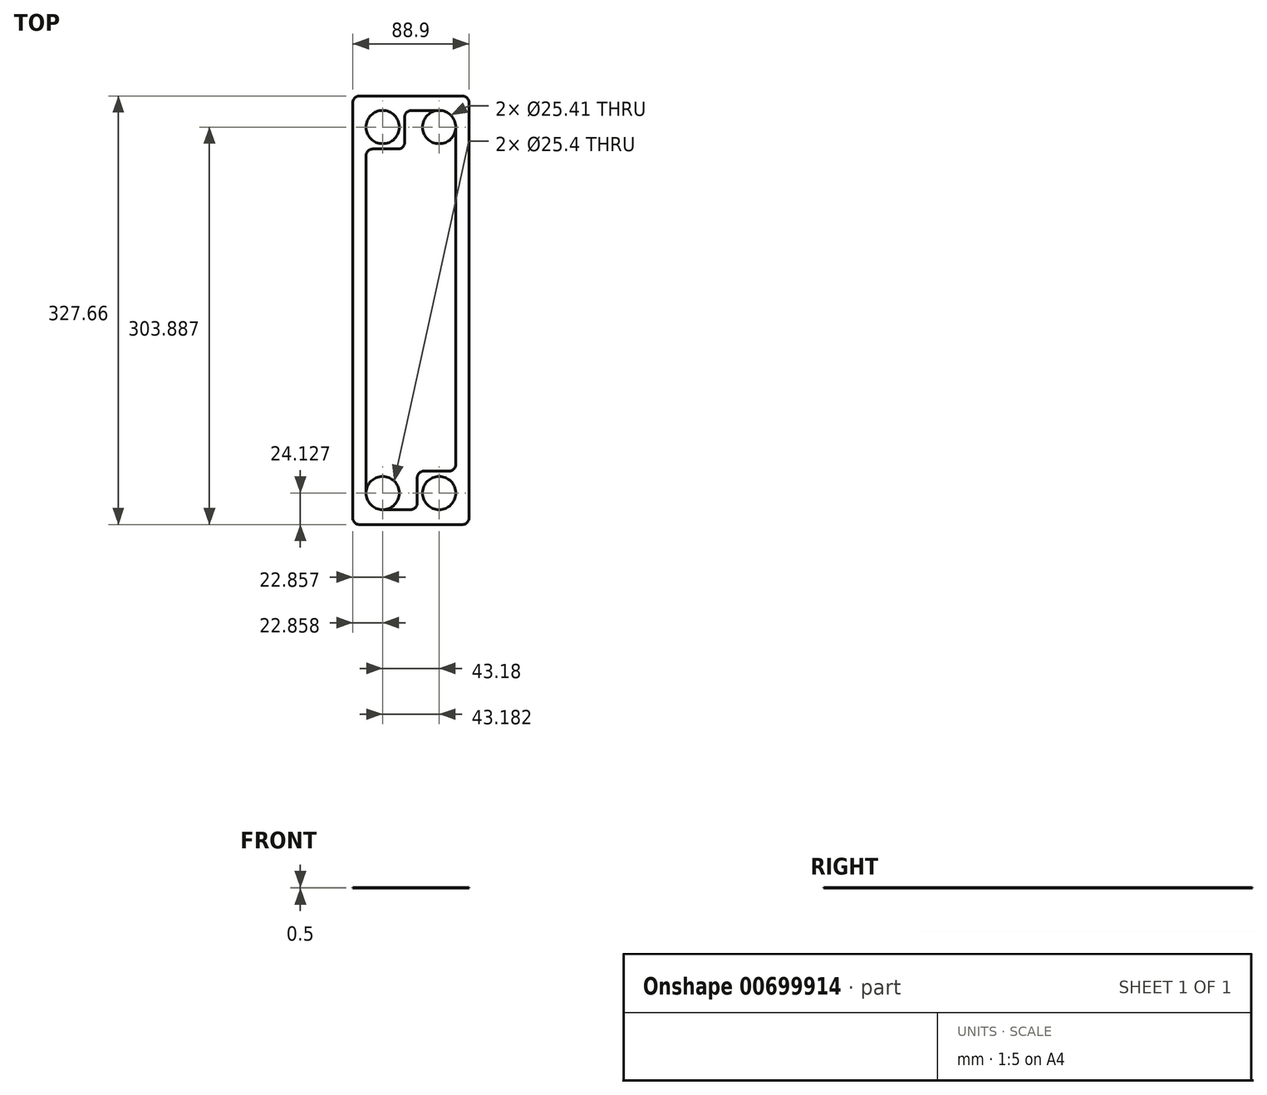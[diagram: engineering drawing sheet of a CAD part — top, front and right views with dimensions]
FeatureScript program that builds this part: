
annotation { "Feature Type Name" : "Feature", "Feature Type Description" : "" }
export const myFeature = defineFeature(function(context is Context, id is Id, definition is map)
    precondition{}
    {
        {
            var Q0;
            Q0=qCreatedBy(makeId("Top.planeOp"),FACE);
            var sketch = newSketch(context, id + "F0", { "sketchPlane" : qUnion([Q0])});
            skLineSegment(sketch, "E0.bottom", {"start": v(28.45, 189.88) * mm, "end": v(-60.45, 189.88) * mm});
            skLineSegment(sketch, "E0.top", {"start": v(28.45, -137.78) * mm, "end": v(-60.45, -137.78) * mm});
            skLineSegment(sketch, "E0.left", {"start": v(28.45, 189.88) * mm, "end": v(28.45, -137.78) * mm});
            skLineSegment(sketch, "E0.right", {"start": v(-60.45, 189.88) * mm, "end": v(-60.45, -137.78) * mm});
            skPoint(sketch, "E1", {"position": v(-37.6, 165.75) * mm});
            skPoint(sketch, "E2", {"position": v(5.59, 165.75) * mm});
            skPoint(sketch, "E3", {"position": v(-34.64, -113.65) * mm});
            skCircle(sketch, "E4.MirrorC", {"center": v(5.59, 166.1) * mm, "radius": 12.7 * mm});
            skCircle(sketch, "E5.MirrorC", {"center": v(-37.6, -113.65) * mm, "radius": 12.7 * mm});
            skCircle(sketch, "E6.MirrorC", {"center": v(-37.6, 166.1) * mm, "radius": 12.7 * mm});
            skCircle(sketch, "E7.MirrorC", {"center": v(5.59, -113.65) * mm, "radius": 12.7 * mm});
            skLineSegment(sketch, "E8", {"start": v(18.3, -96.89) * mm, "end": v(-11.18, -96.89) * mm});
            skLineSegment(sketch, "E9", {"start": v(-11.18, -96.89) * mm, "end": v(-11.18, -126.35) * mm});
            skLineSegment(sketch, "E10", {"start": v(-37.6, -126.35) * mm, "end": v(-11.18, -126.35) * mm});
            skLineSegment(sketch, "E11", {"start": v(18.3, 166.1) * mm, "end": v(18.3, -96.89) * mm});
            skLineSegment(sketch, "E12", {"start": v(5.59, 178.81) * mm, "end": v(-20.83, 178.81) * mm});
            skLineSegment(sketch, "E13", {"start": v(-50.3, -113.65) * mm, "end": v(-50.3, 149.34) * mm});
            skLineSegment(sketch, "E14", {"start": v(-50.3, 149.34) * mm, "end": v(-20.83, 149.34) * mm});
            skLineSegment(sketch, "E15", {"start": v(-20.83, 149.34) * mm, "end": v(-20.83, 178.81) * mm});
            skSolve(sketch);
        }
        {
            var Q0;
            Q0=makeQuery(id+"F0.imprint","IMPRINT",FACE,{"disambiguationData":[TD([[makeQuery(id+"F0.imprint","IMPRINT",EDGE,{"derivedFrom":sQuery(id+"F0.wireOp",EDGE,"E0.bottom")}),1.0]])]});
            var Q1;
            {var subQ13=sQuery(id+"F0.wireOp",EDGE,"E0.left");Q1=makeQuery(id+"F0.imprint","IMPRINT",FACE,{"disambiguationData":[TD([[makeQuery(id+"F0.imprint","IMPRINT",EDGE,{"derivedFrom":subQ13}),-1.0]])]});}
            extrude(context, id + "F1", {"entities" : qUnion([Q0, Q1]), "depth" : 0.5 * mm, "offsetDistance" : 25.4 * mm});
        }
        {
            var Q0;
            {var subQ0=sQuery(id+"F0.wireOp",EDGE,"AVYuMERg-jp42-uW1U-rRQy-gQwv37M2Fl3g");Q0=makeQuery(id+"F0.imprint","IMPRINT",FACE,{"disambiguationData":[TD([[makeQuery(id+"F0.imprint","IMPRINT",EDGE,{"derivedFrom":subQ0}),-1.0]])]});}
            var Q1;
            {var subQ5=sQuery(id+"F0.wireOp",EDGE,"oEbkACiK-kKTr-xMsP-6Dwb-FVCRsFg3JczW");Q1=makeQuery(id+"F0.imprint","IMPRINT",FACE,{"disambiguationData":[TD([[makeQuery(id+"F0.imprint","IMPRINT",EDGE,{"derivedFrom":subQ5}),1.0]])]});}
            var Q2;
            Q2=makeQuery(id+"F0.imprint","IMPRINT",FACE,{"disambiguationData":[TD([[makeQuery(id+"F0.imprint","IMPRINT",EDGE,{"derivedFrom":sQuery(id+"F0.wireOp",EDGE,"E8")}),-1.0]])]});
            extrude(context, id + "F2", {"entities" : qUnion([Q0, Q1, Q2]), "operationType" : NewBodyOperationType.ADD, "depth" : 0 * mm, "offsetDistance" : 25.4 * mm});
        }
        {
            var Q0;
            Q0=makeQuery(id+"F1.opExtrude","SWEPT_EDGE",EDGE,{"disambiguationData":[OSD([sQuery(id+"F0.wireOp",EDGE,"E0.bottom"),sQuery(id+"F0.wireOp",EDGE,"E0.left")])]});
            var Q1;
            Q1=makeQuery(id+"F1.opExtrude","SWEPT_EDGE",EDGE,{"disambiguationData":[OSD([sQuery(id+"F0.wireOp",EDGE,"E0.bottom"),sQuery(id+"F0.wireOp",EDGE,"E0.right")])]});
            var Q2;
            Q2=makeQuery(id+"F1.opExtrude","SWEPT_EDGE",EDGE,{"disambiguationData":[OSD([sQuery(id+"F0.wireOp",EDGE,"E0.top"),sQuery(id+"F0.wireOp",EDGE,"E0.right")])]});
            var Q3;
            Q3=makeQuery(id+"F1.opExtrude","SWEPT_EDGE",EDGE,{"disambiguationData":[OSD([sQuery(id+"F0.wireOp",EDGE,"E0.top"),sQuery(id+"F0.wireOp",EDGE,"E0.left")])]});
            var Q4;
            Q4=makeQuery(id+"F1.opExtrude","SWEPT_EDGE",EDGE,{"disambiguationData":[OSD([sQuery(id+"F0.wireOp",EDGE,"E8"),sQuery(id+"F0.wireOp",EDGE,"E11")])]});
            var Q5;
            Q5=makeQuery(id+"F1.opExtrude","SWEPT_EDGE",EDGE,{"disambiguationData":[OSD([sQuery(id+"F0.wireOp",EDGE,"E8"),sQuery(id+"F0.wireOp",EDGE,"E9")])]});
            var Q6;
            Q6=makeQuery(id+"F1.opExtrude","SWEPT_EDGE",EDGE,{"disambiguationData":[OSD([sQuery(id+"F0.wireOp",EDGE,"E9"),sQuery(id+"F0.wireOp",EDGE,"E10")])]});
            fillet(context, id + "F3", {"entities" : qUnion([Q0, Q1, Q2, Q3, Q4, Q5, Q6]), "radius" : 5.08 * mm, "tangentPropagation" : true, "allowEdgeOverflow" : false});
        }
        {
            var Q0;
            Q0=makeQuery(id+"F1.opExtrude","SWEPT_EDGE",EDGE,{"disambiguationData":[OSD([sQuery(id+"F0.wireOp",EDGE,"oEbkACiK-kKTr-xMsP-6Dwb-FVCRsFg3JczW"),sQuery(id+"F0.wireOp",EDGE,"vKtCIPza-yhRZ-rxRL-Lj7m-7o7ZUmddPepn")])]});
            var Q1;
            Q1=makeQuery(id+"F1.opExtrude","SWEPT_EDGE",EDGE,{"disambiguationData":[OSD([sQuery(id+"F0.wireOp",EDGE,"AVYuMERg-jp42-uW1U-rRQy-gQwv37M2Fl3g"),sQuery(id+"F0.wireOp",EDGE,"vKtCIPza-yhRZ-rxRL-Lj7m-7o7ZUmddPepn")])]});
            var Q2;
            Q2=makeQuery(id+"F1.opExtrude","SWEPT_EDGE",EDGE,{"disambiguationData":[OSD([sQuery(id+"F0.wireOp",EDGE,"pewF66kG-GFMI-JF1X-qAcm-Nm4R1YAsbT13"),sQuery(id+"F0.wireOp",EDGE,"7d1wvmCj-EUQr-oUGu-HAwH-GT3x7ygtlY4H")])]});
            var Q3;
            Q3=makeQuery(id+"F1.opExtrude","SWEPT_EDGE",EDGE,{"disambiguationData":[OSD([sQuery(id+"F0.wireOp",EDGE,"E14"),sQuery(id+"F0.wireOp",EDGE,"E15")])]});
            var Q4;
            Q4=makeQuery(id+"F1.opExtrude","SWEPT_EDGE",EDGE,{"disambiguationData":[OSD([sQuery(id+"F0.wireOp",EDGE,"E13"),sQuery(id+"F0.wireOp",EDGE,"E14")])]});
            var Q5;
            Q5=makeQuery(id+"F1.opExtrude","SWEPT_EDGE",EDGE,{"disambiguationData":[OSD([sQuery(id+"F0.wireOp",EDGE,"E12"),sQuery(id+"F0.wireOp",EDGE,"E15")])]});
            fillet(context, id + "F4", {"entities" : qUnion([Q0, Q1, Q2, Q3, Q4, Q5]), "radius" : 5.08 * mm, "tangentPropagation" : true, "allowEdgeOverflow" : false});
        }
    });
